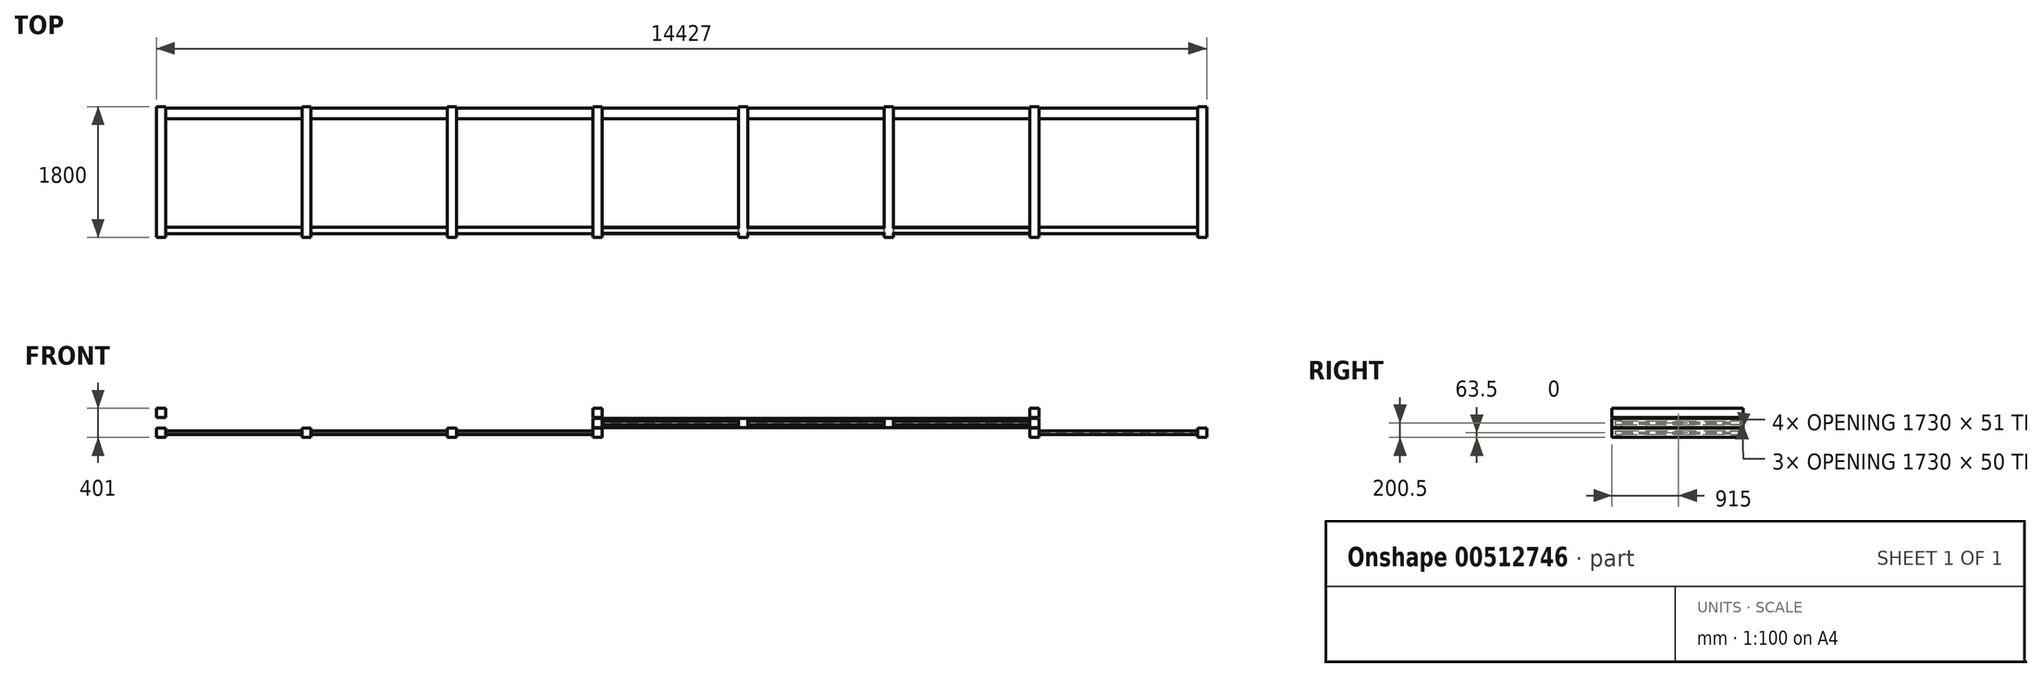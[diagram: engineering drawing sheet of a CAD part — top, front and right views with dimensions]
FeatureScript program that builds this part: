
annotation { "Feature Type Name" : "Feature", "Feature Type Description" : "" }
export const myFeature = defineFeature(function(context is Context, id is Id, definition is map)
    precondition{}
    {
        {
            var Q0;
            Q0=qCreatedBy(makeId("Front.planeOp"),FACE);
            var sketch = newSketch(context, id + "F0", { "sketchPlane" : qUnion([Q0])});
            skLineSegment(sketch, "E0.bottom", {"start": v(2923.43, -12.5) * mm, "end": v(-3076.57, -12.5) * mm});
            skLineSegment(sketch, "E0.top", {"start": v(2923.43, 12.5) * mm, "end": v(-3076.57, 12.5) * mm});
            skLineSegment(sketch, "E0.left", {"start": v(2923.43, -12.5) * mm, "end": v(2923.43, 12.5) * mm});
            skLineSegment(sketch, "E0.right", {"start": v(-3076.57, -12.5) * mm, "end": v(-3076.57, 12.5) * mm});
            skPoint(sketch, "E0.middle", {"position": v(-1076.57, 0) * mm});
            skLineSegment(sketch, "E1.bottom", {"start": v(2986.93, -63.5) * mm, "end": v(2859.93, -63.5) * mm});
            skLineSegment(sketch, "E1.top", {"start": v(2986.93, 63.5) * mm, "end": v(2859.93, 63.5) * mm});
            skLineSegment(sketch, "E1.left", {"start": v(2986.93, -63.5) * mm, "end": v(2986.93, 63.5) * mm});
            skLineSegment(sketch, "E1.right", {"start": v(2859.93, -63.5) * mm, "end": v(2859.93, 63.5) * mm});
            skPoint(sketch, "E1.middle", {"position": v(2923.43, 0) * mm});
            skLineSegment(sketch, "E2.bottom", {"start": v(-3013.07, -63.5) * mm, "end": v(-3140.07, -63.5) * mm});
            skLineSegment(sketch, "E2.top", {"start": v(-3013.07, 63.5) * mm, "end": v(-3140.07, 63.5) * mm});
            skLineSegment(sketch, "E2.left", {"start": v(-3013.07, -63.5) * mm, "end": v(-3013.07, 63.5) * mm});
            skLineSegment(sketch, "E2.right", {"start": v(-3140.07, -63.5) * mm, "end": v(-3140.07, 63.5) * mm});
            skPoint(sketch, "E2.middle", {"position": v(-3076.57, 0) * mm});
            skLineSegment(sketch, "E3.bottom", {"start": v(-1013.07, -63.5) * mm, "end": v(-1140.07, -63.5) * mm});
            skLineSegment(sketch, "E3.top", {"start": v(-1013.07, 63.5) * mm, "end": v(-1140.07, 63.5) * mm});
            skLineSegment(sketch, "E3.left", {"start": v(-1013.07, -63.5) * mm, "end": v(-1013.07, 63.5) * mm});
            skLineSegment(sketch, "E3.right", {"start": v(-1140.07, -63.5) * mm, "end": v(-1140.07, 63.5) * mm});
            skPoint(sketch, "E4.middle", {"position": v(923.43, 0) * mm});
            skLineSegment(sketch, "E5.bottom", {"start": v(986.93, -63.5) * mm, "end": v(859.93, -63.5) * mm});
            skLineSegment(sketch, "E5.top", {"start": v(986.93, 63.5) * mm, "end": v(859.93, 63.5) * mm});
            skLineSegment(sketch, "E5.left", {"start": v(986.93, -63.5) * mm, "end": v(986.93, 63.5) * mm});
            skLineSegment(sketch, "E5.right", {"start": v(859.93, -63.5) * mm, "end": v(859.93, 63.5) * mm});
            skLineSegment(sketch, "E6.bottom", {"start": v(-3013.07, -200.5) * mm, "end": v(-3140.07, -200.5) * mm});
            skLineSegment(sketch, "E6.top", {"start": v(-3013.07, -73.5) * mm, "end": v(-3140.07, -73.5) * mm});
            skLineSegment(sketch, "E6.left", {"start": v(-3013.07, -200.5) * mm, "end": v(-3013.07, -73.5) * mm});
            skLineSegment(sketch, "E6.right", {"start": v(-3140.07, -200.5) * mm, "end": v(-3140.07, -73.5) * mm});
            skPoint(sketch, "E6.middle", {"position": v(-3076.57, -137) * mm});
            skLineSegment(sketch, "E7.1.0.0", {"start": v(-5013.07, -200.5) * mm, "end": v(-5140.07, -200.5) * mm});
            skLineSegment(sketch, "E7.1.0.1", {"start": v(-5140.07, -200.5) * mm, "end": v(-5140.07, -73.5) * mm});
            skLineSegment(sketch, "E7.1.0.2", {"start": v(-5013.07, -73.5) * mm, "end": v(-5140.07, -73.5) * mm});
            skLineSegment(sketch, "E7.1.0.3", {"start": v(-5013.07, -200.5) * mm, "end": v(-5013.07, -73.5) * mm});
            skLineSegment(sketch, "E7.2.0.0", {"start": v(-7013.07, -200.5) * mm, "end": v(-7140.07, -200.5) * mm});
            skLineSegment(sketch, "E7.2.0.1", {"start": v(-7140.07, -200.5) * mm, "end": v(-7140.07, -73.5) * mm});
            skLineSegment(sketch, "E7.2.0.2", {"start": v(-7013.07, -73.5) * mm, "end": v(-7140.07, -73.5) * mm});
            skLineSegment(sketch, "E7.2.0.3", {"start": v(-7013.07, -200.5) * mm, "end": v(-7013.07, -73.5) * mm});
            skLineSegment(sketch, "E7.3.0.0", {"start": v(-9013.07, -200.5) * mm, "end": v(-9140.07, -200.5) * mm});
            skLineSegment(sketch, "E7.3.0.1", {"start": v(-9140.07, -200.5) * mm, "end": v(-9140.07, -73.5) * mm});
            skLineSegment(sketch, "E7.3.0.2", {"start": v(-9013.07, -73.5) * mm, "end": v(-9140.07, -73.5) * mm});
            skLineSegment(sketch, "E7.3.0.3", {"start": v(-9013.07, -200.5) * mm, "end": v(-9013.07, -73.5) * mm});
            skLineSegment(sketch, "E7.direction1", {"start": v(-3140.07, -200.5) * mm, "end": v(-5140.07, -200.5) * mm, "construction": true});
            skLineSegment(sketch, "E8", {"start": v(-9013.07, -126) * mm, "end": v(-3140.07, -126) * mm});
            skLineSegment(sketch, "E9", {"start": v(-3140.07, -148) * mm, "end": v(-9013.07, -148) * mm});
            skLineSegment(sketch, "E10.bottom", {"start": v(2986.93, -200.5) * mm, "end": v(2859.93, -200.5) * mm});
            skLineSegment(sketch, "E10.top", {"start": v(2986.93, -73.5) * mm, "end": v(2859.93, -73.5) * mm});
            skLineSegment(sketch, "E10.left", {"start": v(2986.93, -200.5) * mm, "end": v(2986.93, -73.5) * mm});
            skLineSegment(sketch, "E10.right", {"start": v(2859.93, -200.5) * mm, "end": v(2859.93, -73.5) * mm});
            skPoint(sketch, "E10.middle", {"position": v(2923.43, -137) * mm});
            skPoint(sketch, "E10.cornerSnap0", {"position": v(2986.93, 0) * mm});
            skLineSegment(sketch, "E11.1.0.0", {"start": v(5286.93, -200.5) * mm, "end": v(5159.93, -200.5) * mm});
            skLineSegment(sketch, "E11.1.0.1", {"start": v(5159.93, -200.5) * mm, "end": v(5159.93, -73.5) * mm});
            skLineSegment(sketch, "E11.1.0.2", {"start": v(5286.93, -73.5) * mm, "end": v(5159.93, -73.5) * mm});
            skLineSegment(sketch, "E11.1.0.3", {"start": v(5286.93, -200.5) * mm, "end": v(5286.93, -73.5) * mm});
            skLineSegment(sketch, "E11.direction1", {"start": v(2859.93, -200.5) * mm, "end": v(5159.93, -200.5) * mm, "construction": true});
            skLineSegment(sketch, "E12", {"start": v(2986.93, -126) * mm, "end": v(5159.93, -126) * mm});
            skLineSegment(sketch, "E13", {"start": v(2986.93, -148) * mm, "end": v(5159.93, -148) * mm});
            skLineSegment(sketch, "E14.bottom", {"start": v(2986.93, 73.5) * mm, "end": v(2859.93, 73.5) * mm});
            skLineSegment(sketch, "E14.top", {"start": v(2986.93, 200.5) * mm, "end": v(2859.93, 200.5) * mm});
            skLineSegment(sketch, "E14.left", {"start": v(2986.93, 73.5) * mm, "end": v(2986.93, 200.5) * mm});
            skLineSegment(sketch, "E14.right", {"start": v(2859.93, 73.5) * mm, "end": v(2859.93, 200.5) * mm});
            skPoint(sketch, "E14.middle", {"position": v(2923.43, 137) * mm});
            skLineSegment(sketch, "E15.bottom", {"start": v(-3013.07, 73.5) * mm, "end": v(-3140.07, 73.5) * mm});
            skLineSegment(sketch, "E15.top", {"start": v(-3013.07, 200.5) * mm, "end": v(-3140.07, 200.5) * mm});
            skLineSegment(sketch, "E15.left", {"start": v(-3013.07, 73.5) * mm, "end": v(-3013.07, 200.5) * mm});
            skLineSegment(sketch, "E15.right", {"start": v(-3140.07, 73.5) * mm, "end": v(-3140.07, 200.5) * mm});
            skPoint(sketch, "E15.middle", {"position": v(-3076.57, 137) * mm});
            skLineSegment(sketch, "E16.bottom", {"start": v(-9140.07, 73.5) * mm, "end": v(-9013.07, 73.5) * mm});
            skLineSegment(sketch, "E16.top", {"start": v(-9140.07, 200.5) * mm, "end": v(-9013.07, 200.5) * mm});
            skLineSegment(sketch, "E16.left", {"start": v(-9140.07, 73.5) * mm, "end": v(-9140.07, 200.5) * mm});
            skLineSegment(sketch, "E16.right", {"start": v(-9013.07, 73.5) * mm, "end": v(-9013.07, 200.5) * mm});
            skSolve(sketch);
        }
        {
            var Q0;
            {var subQ0=sQuery(id+"F0.wireOp",EDGE,"E3.right");var subQ1=sQuery(id+"F0.wireOp",EDGE,"E0.bottom");var subQ2=makeQuery(id+"F0.imprint","INTERSECT",VERTEX,{"derivedFrom":[subQ1,subQ0]});Q0=makeQuery(id+"F0.imprint","IMPRINT",FACE,{"disambiguationData":[TD([[makeQuery(id+"F0.imprint","IMPRINT",EDGE,{"disambiguationData":[TD([[subQ2,-1.0]])],"derivedFrom":subQ1}),-1.0]])]});}
            var Q1;
            {var subQ0=sQuery(id+"F0.wireOp",EDGE,"E0.right");Q1=makeQuery(id+"F0.imprint","IMPRINT",FACE,{"disambiguationData":[TD([[makeQuery(id+"F0.imprint","IMPRINT",EDGE,{"derivedFrom":subQ0}),-1.0]])]});}
            var Q2;
            {var subQ0=sQuery(id+"F0.wireOp",EDGE,"E3.left");var subQ1=sQuery(id+"F0.wireOp",EDGE,"E0.bottom");var subQ2=makeQuery(id+"F0.imprint","INTERSECT",VERTEX,{"derivedFrom":[subQ1,subQ0]});Q2=makeQuery(id+"F0.imprint","IMPRINT",FACE,{"disambiguationData":[TD([[makeQuery(id+"F0.imprint","IMPRINT",EDGE,{"disambiguationData":[TD([[subQ2,-1.0]])],"derivedFrom":subQ1}),-1.0]])]});}
            var Q3;
            {var subQ0=sQuery(id+"F0.wireOp",EDGE,"E5.right");var subQ1=sQuery(id+"F0.wireOp",EDGE,"E0.bottom");var subQ2=makeQuery(id+"F0.imprint","INTERSECT",VERTEX,{"derivedFrom":[subQ1,subQ0]});Q3=makeQuery(id+"F0.imprint","IMPRINT",FACE,{"disambiguationData":[TD([[makeQuery(id+"F0.imprint","IMPRINT",EDGE,{"disambiguationData":[TD([[subQ2,-1.0]])],"derivedFrom":subQ1}),-1.0]])]});}
            var Q4;
            {var subQ0=sQuery(id+"F0.wireOp",EDGE,"E5.left");var subQ1=sQuery(id+"F0.wireOp",EDGE,"E0.bottom");var subQ2=makeQuery(id+"F0.imprint","INTERSECT",VERTEX,{"derivedFrom":[subQ1,subQ0]});Q4=makeQuery(id+"F0.imprint","IMPRINT",FACE,{"disambiguationData":[TD([[makeQuery(id+"F0.imprint","IMPRINT",EDGE,{"disambiguationData":[TD([[subQ2,-1.0]])],"derivedFrom":subQ1}),-1.0]])]});}
            var Q5;
            {var subQ0=sQuery(id+"F0.wireOp",EDGE,"E1.right");var subQ1=sQuery(id+"F0.wireOp",EDGE,"E0.bottom");var subQ2=makeQuery(id+"F0.imprint","INTERSECT",VERTEX,{"derivedFrom":[subQ1,subQ0]});Q5=makeQuery(id+"F0.imprint","IMPRINT",FACE,{"disambiguationData":[TD([[makeQuery(id+"F0.imprint","IMPRINT",EDGE,{"disambiguationData":[TD([[subQ2,-1.0]])],"derivedFrom":subQ1}),-1.0]])]});}
            var Q6;
            {var subQ0=sQuery(id+"F0.wireOp",EDGE,"E0.left");Q6=makeQuery(id+"F0.imprint","IMPRINT",FACE,{"disambiguationData":[TD([[makeQuery(id+"F0.imprint","IMPRINT",EDGE,{"derivedFrom":subQ0}),1.0]])]});}
            var Q7;
            {var subQ1=sQuery(id+"F0.wireOp",EDGE,"E0.right");Q7=makeQuery(id+"F0.imprint","IMPRINT",FACE,{"disambiguationData":[TD([[makeQuery(id+"F0.imprint","IMPRINT",EDGE,{"derivedFrom":subQ1}),1.0]])]});}
            var Q8;
            {var subQ5=sQuery(id+"F0.wireOp",EDGE,"E3.bottom");Q8=makeQuery(id+"F0.imprint","IMPRINT",FACE,{"disambiguationData":[TD([[makeQuery(id+"F0.imprint","IMPRINT",EDGE,{"derivedFrom":subQ5}),-1.0]])]});}
            var Q9;
            {var subQ5=sQuery(id+"F0.wireOp",EDGE,"E3.top");Q9=makeQuery(id+"F0.imprint","IMPRINT",FACE,{"disambiguationData":[TD([[makeQuery(id+"F0.imprint","IMPRINT",EDGE,{"derivedFrom":subQ5}),1.0]])]});}
            var Q10;
            {var subQ5=sQuery(id+"F0.wireOp",EDGE,"E5.bottom");Q10=makeQuery(id+"F0.imprint","IMPRINT",FACE,{"disambiguationData":[TD([[makeQuery(id+"F0.imprint","IMPRINT",EDGE,{"derivedFrom":subQ5}),-1.0]])]});}
            var Q11;
            {var subQ5=sQuery(id+"F0.wireOp",EDGE,"E5.top");Q11=makeQuery(id+"F0.imprint","IMPRINT",FACE,{"disambiguationData":[TD([[makeQuery(id+"F0.imprint","IMPRINT",EDGE,{"derivedFrom":subQ5}),1.0]])]});}
            var Q12;
            {var subQ1=sQuery(id+"F0.wireOp",EDGE,"E0.left");Q12=makeQuery(id+"F0.imprint","IMPRINT",FACE,{"disambiguationData":[TD([[makeQuery(id+"F0.imprint","IMPRINT",EDGE,{"derivedFrom":subQ1}),-1.0]])]});}
            extrude(context, id + "F1", {"entities" : qUnion([Q0, Q1, Q2, Q3, Q4, Q5, Q6, Q7, Q8, Q9, Q10, Q11, Q12]), "depth" : 1800 * mm});
        }
        {
            var Q0;
            Q0=makeQuery(id+"F1.opExtrude","SWEPT_FACE",FACE,{"disambiguationData":[OSD([sQuery(id+"F0.wireOp",EDGE,"E2.right")])]});
            var sketch = newSketch(context, id + "F2", { "sketchPlane" : qUnion([Q0])});
            skLineSegment(sketch, "E17.bottom", {"start": v(20, -25) * mm, "end": v(170, -25) * mm});
            skLineSegment(sketch, "E17.top", {"start": v(20, 25) * mm, "end": v(170, 25) * mm});
            skLineSegment(sketch, "E17.left", {"start": v(20, -25) * mm, "end": v(20, 25) * mm});
            skLineSegment(sketch, "E17.right", {"start": v(170, -25) * mm, "end": v(170, 25) * mm});
            skPoint(sketch, "E17.middle", {"position": v(95, 0) * mm});
            skLineSegment(sketch, "E18.bottom", {"start": v(1662, -25) * mm, "end": v(1750, -25) * mm});
            skLineSegment(sketch, "E18.top", {"start": v(1662, 25) * mm, "end": v(1750, 25) * mm});
            skLineSegment(sketch, "E18.left", {"start": v(1662, -25) * mm, "end": v(1662, 25) * mm});
            skLineSegment(sketch, "E18.right", {"start": v(1750, -25) * mm, "end": v(1750, 25) * mm});
            skPoint(sketch, "E18.middle", {"position": v(1706, 0) * mm});
            skPoint(sketch, "E19.startSnap0", {"position": v(1800, 0) * mm});
            skPoint(sketch, "E19.endSnap0", {"position": v(1800, 0) * mm});
            skSolve(sketch);
        }
        {
            var Q0;
            Q0=qSketchRegion(id+"F2",true);
            extrude(context, id + "F3", {"entities" : qUnion([Q0]), "operationType" : NewBodyOperationType.ADD, "oppositeDirection" : true, "depth" : 6000 * mm});
        }
        {
            var Q0;
            {var subQ2=sQuery(id+"F0.wireOp",EDGE,"E1.right");var subQ4=sQuery(id+"F0.wireOp",EDGE,"E0.top");var subQ5=makeQuery(id+"F0.imprint","INTERSECT",VERTEX,{"derivedFrom":[subQ4,subQ2]});Q0=makeQuery(id+"F3.boolean.opBoolean","SPLIT",FACE,{"disambiguationData":[TD([makeQuery(id+"F3.opExtrude","SWEPT_FACE",FACE,{"disambiguationData":[OSD([sQuery(id+"F2.wireOp",EDGE,"E18.right")])]})])],"derivedFrom":makeQuery(id+"F1.opExtrude","SWEPT_FACE",FACE,{"disambiguationData":[OSD([subQ4]),TDD([makeQuery(id+"F0.imprint","IMPRINT",EDGE,{"disambiguationData":[TD([[subQ5,-1.0]])],"derivedFrom":subQ4})])]})});}
            var Q1;
            {var subQ0=sQuery(id+"F0.wireOp",EDGE,"E5.right");var subQ4=sQuery(id+"F0.wireOp",EDGE,"E0.top");var subQ6=makeQuery(id+"F0.imprint","INTERSECT",VERTEX,{"derivedFrom":[subQ4,subQ0]});Q1=makeQuery(id+"F3.boolean.opBoolean","SPLIT",FACE,{"disambiguationData":[TD([makeQuery(id+"F3.opExtrude","SWEPT_FACE",FACE,{"disambiguationData":[OSD([sQuery(id+"F2.wireOp",EDGE,"E18.right")])]})])],"derivedFrom":makeQuery(id+"F1.opExtrude","SWEPT_FACE",FACE,{"disambiguationData":[OSD([subQ4]),TDD([makeQuery(id+"F0.imprint","IMPRINT",EDGE,{"disambiguationData":[TD([[subQ6,-1.0]])],"derivedFrom":subQ4})])]})});}
            var Q2;
            {var subQ0=sQuery(id+"F0.wireOp",EDGE,"E3.right");var subQ4=sQuery(id+"F0.wireOp",EDGE,"E0.top");var subQ6=makeQuery(id+"F0.imprint","INTERSECT",VERTEX,{"derivedFrom":[subQ4,subQ0]});Q2=makeQuery(id+"F3.boolean.opBoolean","SPLIT",FACE,{"disambiguationData":[TD([makeQuery(id+"F3.opExtrude","SWEPT_FACE",FACE,{"disambiguationData":[OSD([sQuery(id+"F2.wireOp",EDGE,"E18.right")])]})])],"derivedFrom":makeQuery(id+"F1.opExtrude","SWEPT_FACE",FACE,{"disambiguationData":[OSD([subQ4]),TDD([makeQuery(id+"F0.imprint","IMPRINT",EDGE,{"disambiguationData":[TD([[subQ6,-1.0]])],"derivedFrom":subQ4})])]})});}
            var Q3;
            {var subQ0=sQuery(id+"F0.wireOp",EDGE,"E3.right");var subQ4=sQuery(id+"F0.wireOp",EDGE,"E0.top");var subQ6=makeQuery(id+"F0.imprint","INTERSECT",VERTEX,{"derivedFrom":[subQ4,subQ0]});Q3=makeQuery(id+"F3.boolean.opBoolean","SPLIT",FACE,{"disambiguationData":[TD([makeQuery(id+"F3.opExtrude","SWEPT_FACE",FACE,{"disambiguationData":[OSD([sQuery(id+"F2.wireOp",EDGE,"E17.left")])]})])],"derivedFrom":makeQuery(id+"F1.opExtrude","SWEPT_FACE",FACE,{"disambiguationData":[OSD([subQ4]),TDD([makeQuery(id+"F0.imprint","IMPRINT",EDGE,{"disambiguationData":[TD([[subQ6,-1.0]])],"derivedFrom":subQ4})])]})});}
            var Q4;
            {var subQ0=sQuery(id+"F0.wireOp",EDGE,"E5.right");var subQ4=sQuery(id+"F0.wireOp",EDGE,"E0.top");var subQ6=makeQuery(id+"F0.imprint","INTERSECT",VERTEX,{"derivedFrom":[subQ4,subQ0]});Q4=makeQuery(id+"F3.boolean.opBoolean","SPLIT",FACE,{"disambiguationData":[TD([makeQuery(id+"F3.opExtrude","SWEPT_FACE",FACE,{"disambiguationData":[OSD([sQuery(id+"F2.wireOp",EDGE,"E17.left")])]})])],"derivedFrom":makeQuery(id+"F1.opExtrude","SWEPT_FACE",FACE,{"disambiguationData":[OSD([subQ4]),TDD([makeQuery(id+"F0.imprint","IMPRINT",EDGE,{"disambiguationData":[TD([[subQ6,-1.0]])],"derivedFrom":subQ4})])]})});}
            var Q5;
            {var subQ2=sQuery(id+"F0.wireOp",EDGE,"E1.right");var subQ4=sQuery(id+"F0.wireOp",EDGE,"E0.top");var subQ5=makeQuery(id+"F0.imprint","INTERSECT",VERTEX,{"derivedFrom":[subQ4,subQ2]});Q5=makeQuery(id+"F3.boolean.opBoolean","SPLIT",FACE,{"disambiguationData":[TD([makeQuery(id+"F3.opExtrude","SWEPT_FACE",FACE,{"disambiguationData":[OSD([sQuery(id+"F2.wireOp",EDGE,"E17.left")])]})])],"derivedFrom":makeQuery(id+"F1.opExtrude","SWEPT_FACE",FACE,{"disambiguationData":[OSD([subQ4]),TDD([makeQuery(id+"F0.imprint","IMPRINT",EDGE,{"disambiguationData":[TD([[subQ5,-1.0]])],"derivedFrom":subQ4})])]})});}
            extrude(context, id + "F4", {"entities" : qUnion([Q0, Q1, Q2, Q3, Q4, Q5]), "operationType" : NewBodyOperationType.REMOVE, "oppositeDirection" : true, "depth" : 50 * mm});
        }
        {
            var Q0;
            Q0=makeQuery(id+"F0.imprint","IMPRINT",FACE,{"disambiguationData":[TD([[makeQuery(id+"F0.imprint","IMPRINT",EDGE,{"derivedFrom":sQuery(id+"F0.wireOp",EDGE,"E15.bottom")}),-1.0]])]});
            var Q1;
            {var subQ1=sQuery(id+"F0.wireOp",EDGE,"E6.bottom");Q1=makeQuery(id+"F0.imprint","IMPRINT",FACE,{"disambiguationData":[TD([[makeQuery(id+"F0.imprint","IMPRINT",EDGE,{"derivedFrom":subQ1}),-1.0]])]});}
            var Q2;
            {var subQ0=sQuery(id+"F0.wireOp",EDGE,"E8");var subQ1=sQuery(id+"F0.wireOp",EDGE,"E6.right");var subQ2=makeQuery(id+"F0.imprint","INTERSECT",VERTEX,{"derivedFrom":[subQ1,subQ0]});Q2=makeQuery(id+"F0.imprint","IMPRINT",FACE,{"disambiguationData":[TD([[makeQuery(id+"F0.imprint","IMPRINT",EDGE,{"disambiguationData":[TD([[subQ2,1.0]])],"derivedFrom":subQ1}),1.0]])]});}
            var Q3;
            {var subQ0=sQuery(id+"F0.wireOp",EDGE,"E7.1.0.0");Q3=makeQuery(id+"F0.imprint","IMPRINT",FACE,{"disambiguationData":[TD([[makeQuery(id+"F0.imprint","IMPRINT",EDGE,{"derivedFrom":subQ0}),-1.0]])]});}
            var Q4;
            {var subQ0=sQuery(id+"F0.wireOp",EDGE,"E9");var subQ1=sQuery(id+"F0.wireOp",EDGE,"E7.1.0.1");var subQ2=makeQuery(id+"F0.imprint","INTERSECT",VERTEX,{"derivedFrom":[subQ1,subQ0]});Q4=makeQuery(id+"F0.imprint","IMPRINT",FACE,{"disambiguationData":[TD([[makeQuery(id+"F0.imprint","IMPRINT",EDGE,{"disambiguationData":[TD([[subQ2,-1.0]])],"derivedFrom":subQ1}),-1.0]])]});}
            var Q5;
            {var subQ0=sQuery(id+"F0.wireOp",EDGE,"E7.1.0.2");Q5=makeQuery(id+"F0.imprint","IMPRINT",FACE,{"disambiguationData":[TD([[makeQuery(id+"F0.imprint","IMPRINT",EDGE,{"derivedFrom":subQ0}),1.0]])]});}
            var Q6;
            {var subQ0=sQuery(id+"F0.wireOp",EDGE,"E9");var subQ1=sQuery(id+"F0.wireOp",EDGE,"E7.1.0.1");var subQ2=makeQuery(id+"F0.imprint","INTERSECT",VERTEX,{"derivedFrom":[subQ1,subQ0]});Q6=makeQuery(id+"F0.imprint","IMPRINT",FACE,{"disambiguationData":[TD([[makeQuery(id+"F0.imprint","IMPRINT",EDGE,{"disambiguationData":[TD([[subQ2,-1.0]])],"derivedFrom":subQ1}),1.0]])]});}
            var Q7;
            {var subQ0=sQuery(id+"F0.wireOp",EDGE,"E7.2.0.0");Q7=makeQuery(id+"F0.imprint","IMPRINT",FACE,{"disambiguationData":[TD([[makeQuery(id+"F0.imprint","IMPRINT",EDGE,{"derivedFrom":subQ0}),-1.0]])]});}
            var Q8;
            {var subQ0=sQuery(id+"F0.wireOp",EDGE,"E9");var subQ1=sQuery(id+"F0.wireOp",EDGE,"E7.2.0.1");var subQ2=makeQuery(id+"F0.imprint","INTERSECT",VERTEX,{"derivedFrom":[subQ1,subQ0]});Q8=makeQuery(id+"F0.imprint","IMPRINT",FACE,{"disambiguationData":[TD([[makeQuery(id+"F0.imprint","IMPRINT",EDGE,{"disambiguationData":[TD([[subQ2,-1.0]])],"derivedFrom":subQ1}),-1.0]])]});}
            var Q9;
            {var subQ0=sQuery(id+"F0.wireOp",EDGE,"E7.2.0.2");Q9=makeQuery(id+"F0.imprint","IMPRINT",FACE,{"disambiguationData":[TD([[makeQuery(id+"F0.imprint","IMPRINT",EDGE,{"derivedFrom":subQ0}),1.0]])]});}
            var Q10;
            Q10=makeQuery(id+"F0.imprint","IMPRINT",FACE,{"disambiguationData":[TD([[makeQuery(id+"F0.imprint","IMPRINT",EDGE,{"derivedFrom":sQuery(id+"F0.wireOp",EDGE,"sggH8rYH-DI2V-JgDC-u7Ei-z58JgbeutMg8.bottom")}),1.0]])]});
            var Q11;
            {var subQ0=sQuery(id+"F0.wireOp",EDGE,"E9");var subQ1=sQuery(id+"F0.wireOp",EDGE,"E7.2.0.1");var subQ2=makeQuery(id+"F0.imprint","INTERSECT",VERTEX,{"derivedFrom":[subQ1,subQ0]});Q11=makeQuery(id+"F0.imprint","IMPRINT",FACE,{"disambiguationData":[TD([[makeQuery(id+"F0.imprint","IMPRINT",EDGE,{"disambiguationData":[TD([[subQ2,-1.0]])],"derivedFrom":subQ1}),1.0]])]});}
            var Q12;
            {var subQ1=sQuery(id+"F0.wireOp",EDGE,"E7.3.0.0");Q12=makeQuery(id+"F0.imprint","IMPRINT",FACE,{"disambiguationData":[TD([[makeQuery(id+"F0.imprint","IMPRINT",EDGE,{"derivedFrom":subQ1}),-1.0]])]});}
            var Q13;
            Q13=makeQuery(id+"F0.imprint","IMPRINT",FACE,{"disambiguationData":[TD([[makeQuery(id+"F0.imprint","IMPRINT",EDGE,{"derivedFrom":sQuery(id+"F0.wireOp",EDGE,"E16.bottom")}),1.0]])]});
            var Q14;
            {var subQ3=sQuery(id+"F0.wireOp",EDGE,"E10.bottom");Q14=makeQuery(id+"F0.imprint","IMPRINT",FACE,{"disambiguationData":[TD([[makeQuery(id+"F0.imprint","IMPRINT",EDGE,{"derivedFrom":subQ3}),-1.0]])]});}
            var Q15;
            Q15=makeQuery(id+"F0.imprint","IMPRINT",FACE,{"disambiguationData":[TD([[makeQuery(id+"F0.imprint","IMPRINT",EDGE,{"derivedFrom":sQuery(id+"F0.wireOp",EDGE,"E14.bottom")}),-1.0]])]});
            var Q16;
            {var subQ0=sQuery(id+"F0.wireOp",EDGE,"E12");Q16=makeQuery(id+"F0.imprint","IMPRINT",FACE,{"disambiguationData":[TD([[makeQuery(id+"F0.imprint","IMPRINT",EDGE,{"derivedFrom":subQ0}),-1.0]])]});}
            var Q17;
            {var subQ4=sQuery(id+"F0.wireOp",EDGE,"E11.1.0.0");Q17=makeQuery(id+"F0.imprint","IMPRINT",FACE,{"disambiguationData":[TD([[makeQuery(id+"F0.imprint","IMPRINT",EDGE,{"derivedFrom":subQ4}),-1.0]])]});}
            extrude(context, id + "F5", {"entities" : qUnion([Q0, Q1, Q2, Q3, Q4, Q5, Q6, Q7, Q8, Q9, Q10, Q11, Q12, Q13, Q14, Q15, Q16, Q17]), "depth" : 1800 * mm});
        }
        {
            var Q0;
            Q0=makeQuery(id+"F5.opExtrude","SWEPT_FACE",FACE,{"disambiguationData":[OSD([sQuery(id+"F0.wireOp",EDGE,"E11.1.0.3")])]});
            var sketch = newSketch(context, id + "F6", { "sketchPlane" : qUnion([Q0])});
            skLineSegment(sketch, "E20.bottom", {"start": v(-20, -111.5) * mm, "end": v(-170, -111.5) * mm});
            skLineSegment(sketch, "E20.top", {"start": v(-20, -162.5) * mm, "end": v(-170, -162.5) * mm});
            skLineSegment(sketch, "E20.left", {"start": v(-20, -111.5) * mm, "end": v(-20, -162.5) * mm});
            skLineSegment(sketch, "E20.right", {"start": v(-170, -111.5) * mm, "end": v(-170, -162.5) * mm});
            skPoint(sketch, "E20.middle", {"position": v(-95, -137) * mm});
            skPoint(sketch, "E20.middle.positionSnap0", {"position": v(0, -137) * mm});
            skPoint(sketch, "E20.centerSnap0", {"position": v(0, -137) * mm});
            skLineSegment(sketch, "E21.bottom", {"start": v(-1662, -111.5) * mm, "end": v(-1750, -111.5) * mm});
            skLineSegment(sketch, "E21.top", {"start": v(-1662, -162.5) * mm, "end": v(-1750, -162.5) * mm});
            skLineSegment(sketch, "E21.left", {"start": v(-1662, -111.5) * mm, "end": v(-1662, -162.5) * mm});
            skLineSegment(sketch, "E21.right", {"start": v(-1750, -111.5) * mm, "end": v(-1750, -162.5) * mm});
            skPoint(sketch, "E21.middle", {"position": v(-1706, -137) * mm});
            skPoint(sketch, "E21.middle.positionSnap0", {"position": v(-1800, -137) * mm});
            skPoint(sketch, "E21.centerSnap0", {"position": v(-1800, -137) * mm});
            skSolve(sketch);
        }
        {
            var Q0;
            Q0=qSketchRegion(id+"F6",true);
            extrude(context, id + "F7", {"entities" : qUnion([Q0]), "operationType" : NewBodyOperationType.ADD, "oppositeDirection" : true, "depth" : 2370 * mm});
        }
        {
            var Q0;
            Q0=makeQuery(id+"F5.opExtrude","SWEPT_FACE",FACE,{"disambiguationData":[OSD([sQuery(id+"F0.wireOp",EDGE,"E7.3.0.1")])]});
            var sketch = newSketch(context, id + "F8", { "sketchPlane" : qUnion([Q0])});
            skLineSegment(sketch, "E22.bottom", {"start": v(20, -162.5) * mm, "end": v(170, -162.5) * mm});
            skLineSegment(sketch, "E22.top", {"start": v(20, -111.5) * mm, "end": v(170, -111.5) * mm});
            skLineSegment(sketch, "E22.left", {"start": v(20, -162.5) * mm, "end": v(20, -111.5) * mm});
            skLineSegment(sketch, "E22.right", {"start": v(170, -162.5) * mm, "end": v(170, -111.5) * mm});
            skPoint(sketch, "E22.middle", {"position": v(95, -137) * mm});
            skPoint(sketch, "E22.middle.positionSnap0", {"position": v(0, -137) * mm});
            skPoint(sketch, "E22.centerSnap0", {"position": v(0, -137) * mm});
            skLineSegment(sketch, "E23.bottom", {"start": v(1662, -162.5) * mm, "end": v(1750, -162.5) * mm});
            skLineSegment(sketch, "E23.top", {"start": v(1662, -111.5) * mm, "end": v(1750, -111.5) * mm});
            skLineSegment(sketch, "E23.left", {"start": v(1662, -162.5) * mm, "end": v(1662, -111.5) * mm});
            skLineSegment(sketch, "E23.right", {"start": v(1750, -162.5) * mm, "end": v(1750, -111.5) * mm});
            skPoint(sketch, "E23.middle", {"position": v(1706, -137) * mm});
            skPoint(sketch, "E23.middle.positionSnap0", {"position": v(1800, -137) * mm});
            skPoint(sketch, "E23.centerSnap0", {"position": v(1800, -137) * mm});
            skSolve(sketch);
        }
        {
            var Q0;
            Q0=qSketchRegion(id+"F8",true);
            extrude(context, id + "F9", {"entities" : qUnion([Q0]), "operationType" : NewBodyOperationType.ADD, "oppositeDirection" : true, "depth" : 6090 * mm});
        }
        {
            var Q0;
            {var subQ0=sQuery(id+"F0.wireOp",EDGE,"E13");Q0=makeQuery(id+"F7.boolean.opBoolean","SPLIT",FACE,{"disambiguationData":[TD([makeQuery(id+"F7.opExtrude","SWEPT_FACE",FACE,{"disambiguationData":[OSD([sQuery(id+"F6.wireOp",EDGE,"E21.right")])]})])],"derivedFrom":makeQuery(id+"F5.opExtrude","SWEPT_FACE",FACE,{"disambiguationData":[OSD([subQ0])]})});}
            var Q1;
            {var subQ0=sQuery(id+"F0.wireOp",EDGE,"E13");Q1=makeQuery(id+"F7.boolean.opBoolean","SPLIT",FACE,{"disambiguationData":[TD([makeQuery(id+"F7.opExtrude","SWEPT_FACE",FACE,{"disambiguationData":[OSD([sQuery(id+"F6.wireOp",EDGE,"E20.left")])]})])],"derivedFrom":makeQuery(id+"F5.opExtrude","SWEPT_FACE",FACE,{"disambiguationData":[OSD([subQ0])]})});}
            var Q2;
            {var subQ0=sQuery(id+"F0.wireOp",EDGE,"E9");var subQ3=sQuery(id+"F0.wireOp",EDGE,"E6.right");var subQ5=makeQuery(id+"F0.imprint","INTERSECT",VERTEX,{"derivedFrom":[subQ3,subQ0]});Q2=makeQuery(id+"F9.boolean.opBoolean","SPLIT",FACE,{"disambiguationData":[TD([makeQuery(id+"F9.opExtrude","SWEPT_FACE",FACE,{"disambiguationData":[OSD([sQuery(id+"F8.wireOp",EDGE,"E23.right")])]})])],"derivedFrom":makeQuery(id+"F5.opExtrude","SWEPT_FACE",FACE,{"disambiguationData":[OSD([subQ0]),TDD([makeQuery(id+"F0.imprint","IMPRINT",EDGE,{"disambiguationData":[TD([[subQ5,-1.0]])],"derivedFrom":subQ0})])]})});}
            var Q3;
            {var subQ0=sQuery(id+"F0.wireOp",EDGE,"E9");var subQ3=sQuery(id+"F0.wireOp",EDGE,"E7.1.0.1");var subQ6=makeQuery(id+"F0.imprint","INTERSECT",VERTEX,{"derivedFrom":[subQ3,subQ0]});Q3=makeQuery(id+"F9.boolean.opBoolean","SPLIT",FACE,{"disambiguationData":[TD([makeQuery(id+"F9.opExtrude","SWEPT_FACE",FACE,{"disambiguationData":[OSD([sQuery(id+"F8.wireOp",EDGE,"E23.right")])]})])],"derivedFrom":makeQuery(id+"F5.opExtrude","SWEPT_FACE",FACE,{"disambiguationData":[OSD([subQ0]),TDD([makeQuery(id+"F0.imprint","IMPRINT",EDGE,{"disambiguationData":[TD([[subQ6,-1.0]])],"derivedFrom":subQ0})])]})});}
            var Q4;
            {var subQ0=sQuery(id+"F0.wireOp",EDGE,"E9");var subQ1=sQuery(id+"F0.wireOp",EDGE,"E7.3.0.3");var subQ5=makeQuery(id+"F0.imprint","INTERSECT",VERTEX,{"derivedFrom":[subQ1,subQ0]});Q4=makeQuery(id+"F9.boolean.opBoolean","SPLIT",FACE,{"disambiguationData":[TD([makeQuery(id+"F9.opExtrude","SWEPT_FACE",FACE,{"disambiguationData":[OSD([sQuery(id+"F8.wireOp",EDGE,"E23.right")])]})])],"derivedFrom":makeQuery(id+"F5.opExtrude","SWEPT_FACE",FACE,{"disambiguationData":[OSD([subQ0]),TDD([makeQuery(id+"F0.imprint","IMPRINT",EDGE,{"disambiguationData":[TD([[subQ5,1.0]])],"derivedFrom":subQ0})])]})});}
            var Q5;
            {var subQ0=sQuery(id+"F0.wireOp",EDGE,"E9");var subQ1=sQuery(id+"F0.wireOp",EDGE,"E7.3.0.3");var subQ6=makeQuery(id+"F0.imprint","INTERSECT",VERTEX,{"derivedFrom":[subQ1,subQ0]});Q5=makeQuery(id+"F9.boolean.opBoolean","SPLIT",FACE,{"disambiguationData":[TD([makeQuery(id+"F9.opExtrude","SWEPT_FACE",FACE,{"disambiguationData":[OSD([sQuery(id+"F8.wireOp",EDGE,"E22.left")])]})])],"derivedFrom":makeQuery(id+"F5.opExtrude","SWEPT_FACE",FACE,{"disambiguationData":[OSD([subQ0]),TDD([makeQuery(id+"F0.imprint","IMPRINT",EDGE,{"disambiguationData":[TD([[subQ6,1.0]])],"derivedFrom":subQ0})])]})});}
            var Q6;
            {var subQ0=sQuery(id+"F0.wireOp",EDGE,"E9");var subQ3=sQuery(id+"F0.wireOp",EDGE,"E7.1.0.1");var subQ5=makeQuery(id+"F0.imprint","INTERSECT",VERTEX,{"derivedFrom":[subQ3,subQ0]});Q6=makeQuery(id+"F9.boolean.opBoolean","SPLIT",FACE,{"disambiguationData":[TD([makeQuery(id+"F9.opExtrude","SWEPT_FACE",FACE,{"disambiguationData":[OSD([sQuery(id+"F8.wireOp",EDGE,"E22.left")])]})])],"derivedFrom":makeQuery(id+"F5.opExtrude","SWEPT_FACE",FACE,{"disambiguationData":[OSD([subQ0]),TDD([makeQuery(id+"F0.imprint","IMPRINT",EDGE,{"disambiguationData":[TD([[subQ5,-1.0]])],"derivedFrom":subQ0})])]})});}
            var Q7;
            {var subQ0=sQuery(id+"F0.wireOp",EDGE,"E9");var subQ3=sQuery(id+"F0.wireOp",EDGE,"E6.right");var subQ6=makeQuery(id+"F0.imprint","INTERSECT",VERTEX,{"derivedFrom":[subQ3,subQ0]});Q7=makeQuery(id+"F9.boolean.opBoolean","SPLIT",FACE,{"disambiguationData":[TD([makeQuery(id+"F9.opExtrude","SWEPT_FACE",FACE,{"disambiguationData":[OSD([sQuery(id+"F8.wireOp",EDGE,"E22.left")])]})])],"derivedFrom":makeQuery(id+"F5.opExtrude","SWEPT_FACE",FACE,{"disambiguationData":[OSD([subQ0]),TDD([makeQuery(id+"F0.imprint","IMPRINT",EDGE,{"disambiguationData":[TD([[subQ6,-1.0]])],"derivedFrom":subQ0})])]})});}
            extrude(context, id + "F10", {"entities" : qUnion([Q0, Q1, Q2, Q3, Q4, Q5, Q6, Q7]), "operationType" : NewBodyOperationType.REMOVE, "oppositeDirection" : true, "depth" : 50 * mm});
        }
        {
            var Q0;
            Q0=makeQuery(id+"F1.opExtrude","SWEPT_FACE",FACE,{"disambiguationData":[OSD([sQuery(id+"F0.wireOp",EDGE,"E1.left")])]});
            var sketch = newSketch(context, id + "F11", { "sketchPlane" : qUnion([Q0])});
            skLineSegment(sketch, "E24.bottom", {"start": v(-1662, 25.5) * mm, "end": v(-1750, 25.5) * mm});
            skLineSegment(sketch, "E24.top", {"start": v(-1662, -25.5) * mm, "end": v(-1750, -25.5) * mm});
            skLineSegment(sketch, "E24.left", {"start": v(-1662, 25.5) * mm, "end": v(-1662, -25.5) * mm});
            skLineSegment(sketch, "E24.right", {"start": v(-1750, 25.5) * mm, "end": v(-1750, -25.5) * mm});
            skPoint(sketch, "E24.middle", {"position": v(-1706, 0) * mm});
            skPoint(sketch, "E24.middle.positionSnap0", {"position": v(-1800, 0) * mm});
            skPoint(sketch, "E24.centerSnap0", {"position": v(-1800, 0) * mm});
            skPoint(sketch, "E25.endSnap0", {"position": v(-1706, -25.5) * mm});
            skLineSegment(sketch, "E26.bottom", {"start": v(-1739, -63.5) * mm, "end": v(-1673, -63.5) * mm});
            skLineSegment(sketch, "E26.top", {"start": v(-1739, 63.5) * mm, "end": v(-1673, 63.5) * mm});
            skLineSegment(sketch, "E26.left", {"start": v(-1744, -58.5) * mm, "end": v(-1744, 58.5) * mm});
            skLineSegment(sketch, "E26.right", {"start": v(-1668, -58.5) * mm, "end": v(-1668, 58.5) * mm});
            skPoint(sketch, "E27.visualSharp", {"position": v(-1744, -63.5) * mm});
            skArc(sketch, "E27.filletArc", {"start": v(-1744, -58.5) * mm, "mid": v(-1742.54, -62.04) * mm, "end": v(-1739, -63.5) * mm});
            skPoint(sketch, "E28.visualSharp", {"position": v(-1668, -63.5) * mm});
            skArc(sketch, "E28.filletArc", {"start": v(-1673, -63.5) * mm, "mid": v(-1669.46, -62.04) * mm, "end": v(-1668, -58.5) * mm});
            skPoint(sketch, "E29.visualSharp", {"position": v(-1668, 63.5) * mm});
            skArc(sketch, "E29.filletArc", {"start": v(-1668, 58.5) * mm, "mid": v(-1669.46, 62.04) * mm, "end": v(-1673, 63.5) * mm});
            skPoint(sketch, "E30.visualSharp", {"position": v(-1744, 63.5) * mm});
            skArc(sketch, "E30.filletArc", {"start": v(-1739, 63.5) * mm, "mid": v(-1742.54, 62.04) * mm, "end": v(-1744, 58.5) * mm});
            skSolve(sketch);
        }
        {
            var Q0;
            Q0=makeQuery(id+"F11.imprint","IMPRINT",FACE,{"disambiguationData":[TD([[makeQuery(id+"F11.imprint","IMPRINT",EDGE,{"derivedFrom":sQuery(id+"F11.wireOp",EDGE,"E26.bottom")}),1.0]])]});
            var Q1;
            Q1=makeQuery(id+"F11.imprint","IMPRINT",FACE,{"disambiguationData":[TD([[makeQuery(id+"F11.imprint","IMPRINT",EDGE,{"derivedFrom":sQuery(id+"F11.wireOp",EDGE,"E26.top")}),-1.0]])]});
            extrude(context, id + "F12", {"entities" : qUnion([Q0, Q1]), "operationType" : NewBodyOperationType.ADD, "oppositeDirection" : true, "depth" : 6000 * mm});
        }
    });
